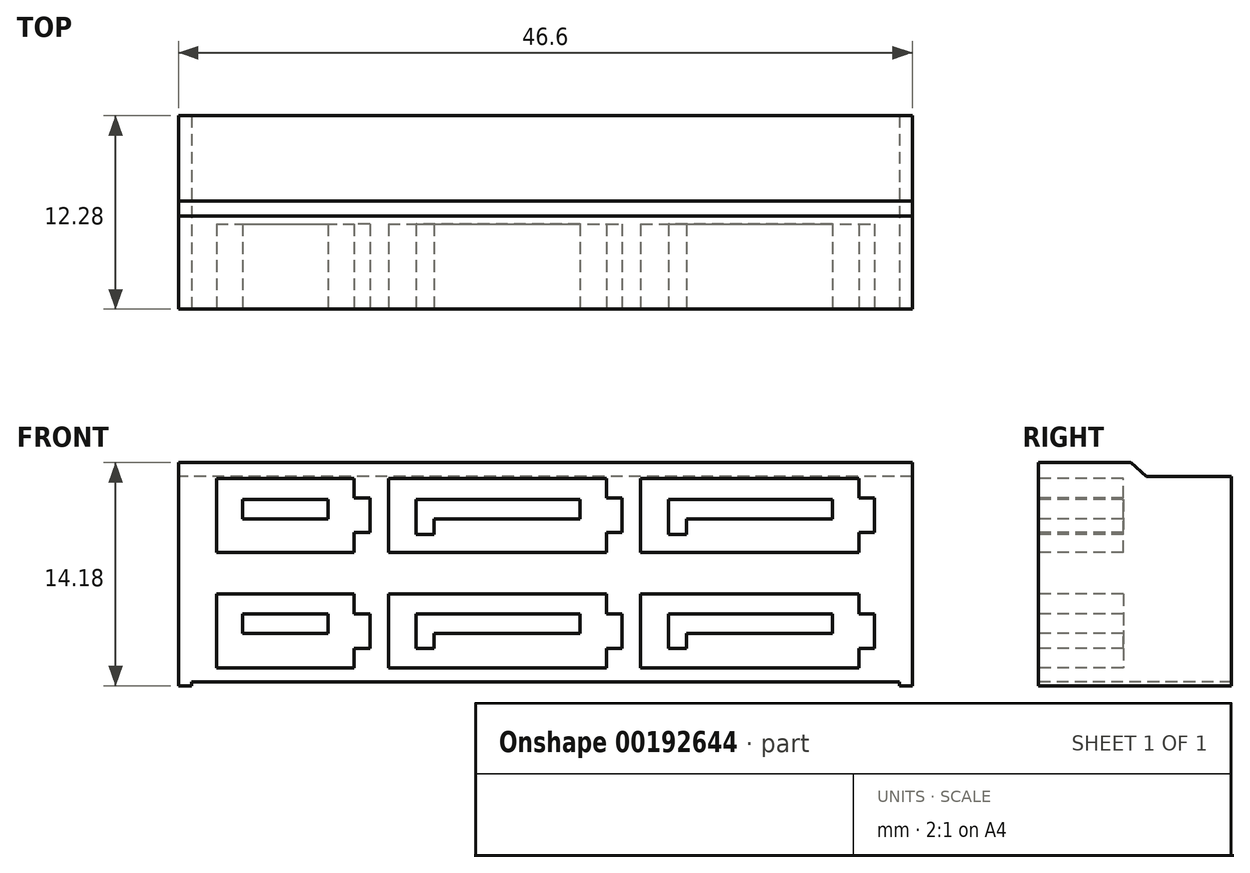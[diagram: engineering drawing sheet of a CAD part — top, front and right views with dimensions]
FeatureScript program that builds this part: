
annotation { "Feature Type Name" : "Feature", "Feature Type Description" : "" }
export const myFeature = defineFeature(function(context is Context, id is Id, definition is map)
    precondition{}
    {
        {
            var Q0;
            Q0=qCreatedBy(makeId("Right.planeOp"),FACE);
            var sketch = newSketch(context, id + "F0", { "sketchPlane" : qUnion([Q0])});
            skLineSegment(sketch, "E0", {"start": v(-6.14, 14.18) * mm, "end": v(-6.14, 0) * mm});
            skLineSegment(sketch, "E1", {"start": v(-6.14, 0) * mm, "end": v(6.14, 0) * mm});
            skLineSegment(sketch, "E2", {"start": v(6.14, 0) * mm, "end": v(6.14, 13.3) * mm});
            skLineSegment(sketch, "E3", {"start": v(6.14, 13.3) * mm, "end": v(0.73, 13.3) * mm});
            skLineSegment(sketch, "E4", {"start": v(0.73, 13.3) * mm, "end": v(-0.24, 14.18) * mm});
            skLineSegment(sketch, "E5", {"start": v(-0.24, 14.18) * mm, "end": v(-6.14, 14.18) * mm});
            skSolve(sketch);
        }
        {
            var Q0;
            Q0 = qSketchRegion(id + "F0", true);
            extrude(context, id + "F1", {"entities" : qUnion([Q0]), "endBound" : BoundingType.SYMMETRIC, "depth" : 46.6 * mm});
        }
        {
            var Q0;
            Q0=makeQuery(id+"F1.opExtrude","SWEPT_FACE",FACE,{"disambiguationData":[OSD([sQuery(id+"F0.wireOp",EDGE,"E0")])]});
            var sketch = newSketch(context, id + "F2", { "sketchPlane" : qUnion([Q0])});
            skLineSegment(sketch, "E6.0", {"start": v(22.47, 0.25) * mm, "end": v(-22.47, 0.25) * mm});
            skLineSegment(sketch, "E7.0", {"start": v(-22.47, 0.25) * mm, "end": v(-22.47, 0) * mm});
            skLineSegment(sketch, "E8.0", {"start": v(22.47, 0.25) * mm, "end": v(22.47, 0) * mm});
            skLineSegment(sketch, "E9.0", {"start": v(22.47, 0) * mm, "end": v(-22.47, 0) * mm});
            skPoint(sketch, "E10.orphan", {"position": v(23.3, 0) * mm});
            skPoint(sketch, "E11.orphan", {"position": v(-23.3, 0) * mm});
            skSolve(sketch);
        }
        {
            var Q0;
            Q0 = qSketchRegion(id + "F2", true);
            extrude(context, id + "F3", {"entities" : qUnion([Q0]), "operationType" : NewBodyOperationType.REMOVE, "endBound" : BoundingType.THROUGH_ALL, "oppositeDirection" : true, "depth" : 25.4 * mm});
        }
        {
            var Q0;
            Q0=makeQuery(id+"F1.opExtrude","SWEPT_FACE",FACE,{"disambiguationData":[OSD([sQuery(id+"F0.wireOp",EDGE,"E0")])]});
            var sketch = newSketch(context, id + "F4", { "sketchPlane" : qUnion([Q0])});
            skLineSegment(sketch, "E12.bottom", {"start": v(-20.9, 5.82) * mm, "end": v(-12.15, 5.82) * mm});
            skLineSegment(sketch, "E12.top", {"start": v(-20.9, 1.12) * mm, "end": v(-12.15, 1.12) * mm});
            skLineSegment(sketch, "E12.left", {"start": v(-20.9, 5.82) * mm, "end": v(-20.9, 1.12) * mm});
            skLineSegment(sketch, "E12.right", {"start": v(-12.15, 5.82) * mm, "end": v(-12.15, 4.57) * mm});
            skLineSegment(sketch, "E13.bottom", {"start": v(-9.97, 1.12) * mm, "end": v(3.88, 1.12) * mm});
            skLineSegment(sketch, "E13.top", {"start": v(-9.97, 5.82) * mm, "end": v(3.88, 5.82) * mm});
            skLineSegment(sketch, "E13.left", {"start": v(-9.97, 1.12) * mm, "end": v(-9.97, 5.82) * mm});
            skLineSegment(sketch, "E13.right", {"start": v(3.88, 1.12) * mm, "end": v(3.88, 2.37) * mm});
            skLineSegment(sketch, "E14.bottom", {"start": v(6.05, 1.12) * mm, "end": v(19.9, 1.12) * mm});
            skLineSegment(sketch, "E14.top", {"start": v(6.05, 5.82) * mm, "end": v(19.9, 5.82) * mm});
            skLineSegment(sketch, "E14.left", {"start": v(6.05, 1.12) * mm, "end": v(6.05, 5.82) * mm});
            skLineSegment(sketch, "E14.right", {"start": v(19.9, 1.12) * mm, "end": v(19.9, 2.37) * mm});
            skLineSegment(sketch, "E15.bottom", {"start": v(19.9, 8.48) * mm, "end": v(6.05, 8.48) * mm});
            skLineSegment(sketch, "E15.top", {"start": v(19.9, 13.18) * mm, "end": v(6.05, 13.18) * mm});
            skLineSegment(sketch, "E15.left", {"start": v(19.9, 8.48) * mm, "end": v(19.9, 9.73) * mm});
            skLineSegment(sketch, "E15.right", {"start": v(6.05, 8.48) * mm, "end": v(6.05, 13.18) * mm});
            skLineSegment(sketch, "E16.bottom", {"start": v(3.88, 13.18) * mm, "end": v(-9.98, 13.18) * mm});
            skLineSegment(sketch, "E16.top", {"start": v(3.88, 8.48) * mm, "end": v(-9.97, 8.48) * mm});
            skLineSegment(sketch, "E16.left", {"start": v(3.88, 13.18) * mm, "end": v(3.88, 11.93) * mm});
            skLineSegment(sketch, "E16.right", {"start": v(-9.98, 13.18) * mm, "end": v(-9.97, 8.48) * mm});
            skLineSegment(sketch, "E17.bottom", {"start": v(-12.15, 13.18) * mm, "end": v(-20.9, 13.18) * mm});
            skLineSegment(sketch, "E17.top", {"start": v(-12.15, 8.48) * mm, "end": v(-20.9, 8.48) * mm});
            skLineSegment(sketch, "E17.left", {"start": v(-12.15, 13.18) * mm, "end": v(-12.15, 11.93) * mm});
            skLineSegment(sketch, "E17.right", {"start": v(-20.9, 13.18) * mm, "end": v(-20.9, 8.48) * mm});
            skLineSegment(sketch, "E18", {"start": v(-23.3, 7.1) * mm, "end": v(23.3, 7.1) * mm, "construction": true});
            skLineSegment(sketch, "E19", {"start": v(-12.15, 4.57) * mm, "end": v(-11.15, 4.57) * mm});
            skLineSegment(sketch, "E20", {"start": v(-11.15, 4.57) * mm, "end": v(-11.15, 2.37) * mm});
            skLineSegment(sketch, "E21", {"start": v(-11.15, 2.37) * mm, "end": v(-12.15, 2.37) * mm});
            skLineSegment(sketch, "E22.bottom", {"start": v(-12.15, 11.93) * mm, "end": v(-11.15, 11.93) * mm});
            skLineSegment(sketch, "E22.top", {"start": v(-12.15, 9.73) * mm, "end": v(-11.15, 9.73) * mm});
            skLineSegment(sketch, "E22.right", {"start": v(-11.15, 11.93) * mm, "end": v(-11.15, 9.73) * mm});
            skLineSegment(sketch, "E23.bottom", {"start": v(3.88, 11.93) * mm, "end": v(4.88, 11.93) * mm});
            skLineSegment(sketch, "E23.top", {"start": v(3.88, 9.73) * mm, "end": v(4.88, 9.73) * mm});
            skLineSegment(sketch, "E23.right", {"start": v(4.88, 11.93) * mm, "end": v(4.88, 9.73) * mm});
            skLineSegment(sketch, "E24.bottom", {"start": v(3.88, 4.57) * mm, "end": v(4.88, 4.57) * mm});
            skLineSegment(sketch, "E24.top", {"start": v(3.88, 2.37) * mm, "end": v(4.88, 2.37) * mm});
            skLineSegment(sketch, "E24.right", {"start": v(4.88, 4.57) * mm, "end": v(4.88, 2.37) * mm});
            skLineSegment(sketch, "E25.bottom", {"start": v(19.9, 2.37) * mm, "end": v(20.9, 2.37) * mm});
            skLineSegment(sketch, "E25.top", {"start": v(19.9, 4.57) * mm, "end": v(20.9, 4.57) * mm});
            skLineSegment(sketch, "E25.right", {"start": v(20.9, 2.37) * mm, "end": v(20.9, 4.57) * mm});
            skLineSegment(sketch, "E26.bottom", {"start": v(19.9, 9.73) * mm, "end": v(20.9, 9.73) * mm});
            skLineSegment(sketch, "E26.top", {"start": v(19.9, 11.93) * mm, "end": v(20.9, 11.93) * mm});
            skLineSegment(sketch, "E26.right", {"start": v(20.9, 9.73) * mm, "end": v(20.9, 11.93) * mm});
            skLineSegment(sketch, "E27.trimOffspring", {"start": v(-12.15, 2.37) * mm, "end": v(-12.15, 1.12) * mm});
            skLineSegment(sketch, "E28.trimOffspring", {"start": v(-12.15, 9.73) * mm, "end": v(-12.15, 8.48) * mm});
            skLineSegment(sketch, "E29.trimOffspring", {"start": v(3.88, 9.73) * mm, "end": v(3.88, 8.48) * mm});
            skLineSegment(sketch, "E30.trimOffspring", {"start": v(3.88, 4.57) * mm, "end": v(3.88, 5.82) * mm});
            skLineSegment(sketch, "E31.trimOffspring", {"start": v(19.9, 4.57) * mm, "end": v(19.9, 5.82) * mm});
            skLineSegment(sketch, "E32.trimOffspring", {"start": v(19.9, 11.93) * mm, "end": v(19.9, 13.18) * mm});
            skLineSegment(sketch, "E33", {"start": v(6.05, 3.47) * mm, "end": v(4.88, 3.47) * mm, "construction": true});
            skLineSegment(sketch, "E34", {"start": v(-9.97, 3.47) * mm, "end": v(-11.15, 3.47) * mm, "construction": true});
            skLineSegment(sketch, "E35.bottom", {"start": v(-19.25, 4.57) * mm, "end": v(-13.8, 4.57) * mm});
            skLineSegment(sketch, "E35.top", {"start": v(-19.25, 3.34) * mm, "end": v(-13.8, 3.34) * mm});
            skLineSegment(sketch, "E35.left", {"start": v(-19.25, 4.57) * mm, "end": v(-19.25, 3.34) * mm});
            skLineSegment(sketch, "E35.right", {"start": v(-13.8, 4.57) * mm, "end": v(-13.8, 3.34) * mm});
            skLineSegment(sketch, "E36", {"start": v(-8.21, 4.57) * mm, "end": v(-8.21, 2.37) * mm});
            skLineSegment(sketch, "E37", {"start": v(-8.21, 2.37) * mm, "end": v(-7.07, 2.37) * mm});
            skLineSegment(sketch, "E38", {"start": v(-7.07, 2.37) * mm, "end": v(-7.07, 3.34) * mm});
            skLineSegment(sketch, "E39", {"start": v(-7.07, 3.34) * mm, "end": v(2.2, 3.34) * mm});
            skLineSegment(sketch, "E40", {"start": v(2.2, 3.34) * mm, "end": v(2.2, 4.57) * mm});
            skLineSegment(sketch, "E41", {"start": v(2.2, 4.57) * mm, "end": v(-8.21, 4.57) * mm});
            skLineSegment(sketch, "E42", {"start": v(-16.53, 4.57) * mm, "end": v(-16.53, 3.34) * mm, "construction": true});
            skLineSegment(sketch, "E43.0.1.0", {"start": v(-19.25, 11.82) * mm, "end": v(-19.25, 10.6) * mm});
            skLineSegment(sketch, "E43.0.1.1", {"start": v(-19.25, 11.82) * mm, "end": v(-13.8, 11.82) * mm});
            skLineSegment(sketch, "E43.0.1.2", {"start": v(-19.25, 10.6) * mm, "end": v(-13.8, 10.6) * mm});
            skLineSegment(sketch, "E43.0.1.4", {"start": v(-13.8, 11.82) * mm, "end": v(-13.8, 10.6) * mm});
            skLineSegment(sketch, "E43.0.1.5", {"start": v(2.2, 11.82) * mm, "end": v(-8.21, 11.82) * mm});
            skLineSegment(sketch, "E43.0.1.6", {"start": v(-7.07, 10.6) * mm, "end": v(2.2, 10.6) * mm});
            skLineSegment(sketch, "E43.0.1.7", {"start": v(-8.21, 11.82) * mm, "end": v(-8.21, 9.62) * mm});
            skLineSegment(sketch, "E43.0.1.8", {"start": v(2.2, 10.6) * mm, "end": v(2.2, 11.82) * mm});
            skLineSegment(sketch, "E43.0.1.9", {"start": v(-7.07, 9.62) * mm, "end": v(-7.07, 10.6) * mm});
            skLineSegment(sketch, "E43.0.1.10", {"start": v(-8.21, 9.62) * mm, "end": v(-7.07, 9.62) * mm});
            skLineSegment(sketch, "E44", {"start": v(7.81, 4.57) * mm, "end": v(7.81, 2.37) * mm});
            skLineSegment(sketch, "E45", {"start": v(7.81, 2.37) * mm, "end": v(8.96, 2.37) * mm});
            skLineSegment(sketch, "E46", {"start": v(8.96, 2.37) * mm, "end": v(8.96, 3.34) * mm});
            skLineSegment(sketch, "E47", {"start": v(8.96, 3.34) * mm, "end": v(18.22, 3.34) * mm});
            skLineSegment(sketch, "E48", {"start": v(18.22, 3.34) * mm, "end": v(18.22, 4.57) * mm});
            skLineSegment(sketch, "E49", {"start": v(18.22, 4.57) * mm, "end": v(7.81, 4.57) * mm});
            skLineSegment(sketch, "E50.0.1.5", {"start": v(18.22, 11.82) * mm, "end": v(7.81, 11.82) * mm});
            skLineSegment(sketch, "E50.0.1.6", {"start": v(8.96, 10.6) * mm, "end": v(18.22, 10.6) * mm});
            skLineSegment(sketch, "E50.0.1.7", {"start": v(7.81, 11.82) * mm, "end": v(7.81, 9.62) * mm});
            skLineSegment(sketch, "E50.0.1.8", {"start": v(18.22, 10.6) * mm, "end": v(18.22, 11.82) * mm});
            skLineSegment(sketch, "E50.0.1.9", {"start": v(8.96, 9.62) * mm, "end": v(8.96, 10.6) * mm});
            skLineSegment(sketch, "E50.0.1.10", {"start": v(7.81, 9.62) * mm, "end": v(8.96, 9.62) * mm});
            skSolve(sketch);
        }
        {
            var Q0;
            Q0 = qSketchRegion(id + "F4", true);
            extrude(context, id + "F5", {"entities" : qUnion([Q0]), "operationType" : NewBodyOperationType.REMOVE, "oppositeDirection" : true, "depth" : 5.4 * mm});
        }
    });
